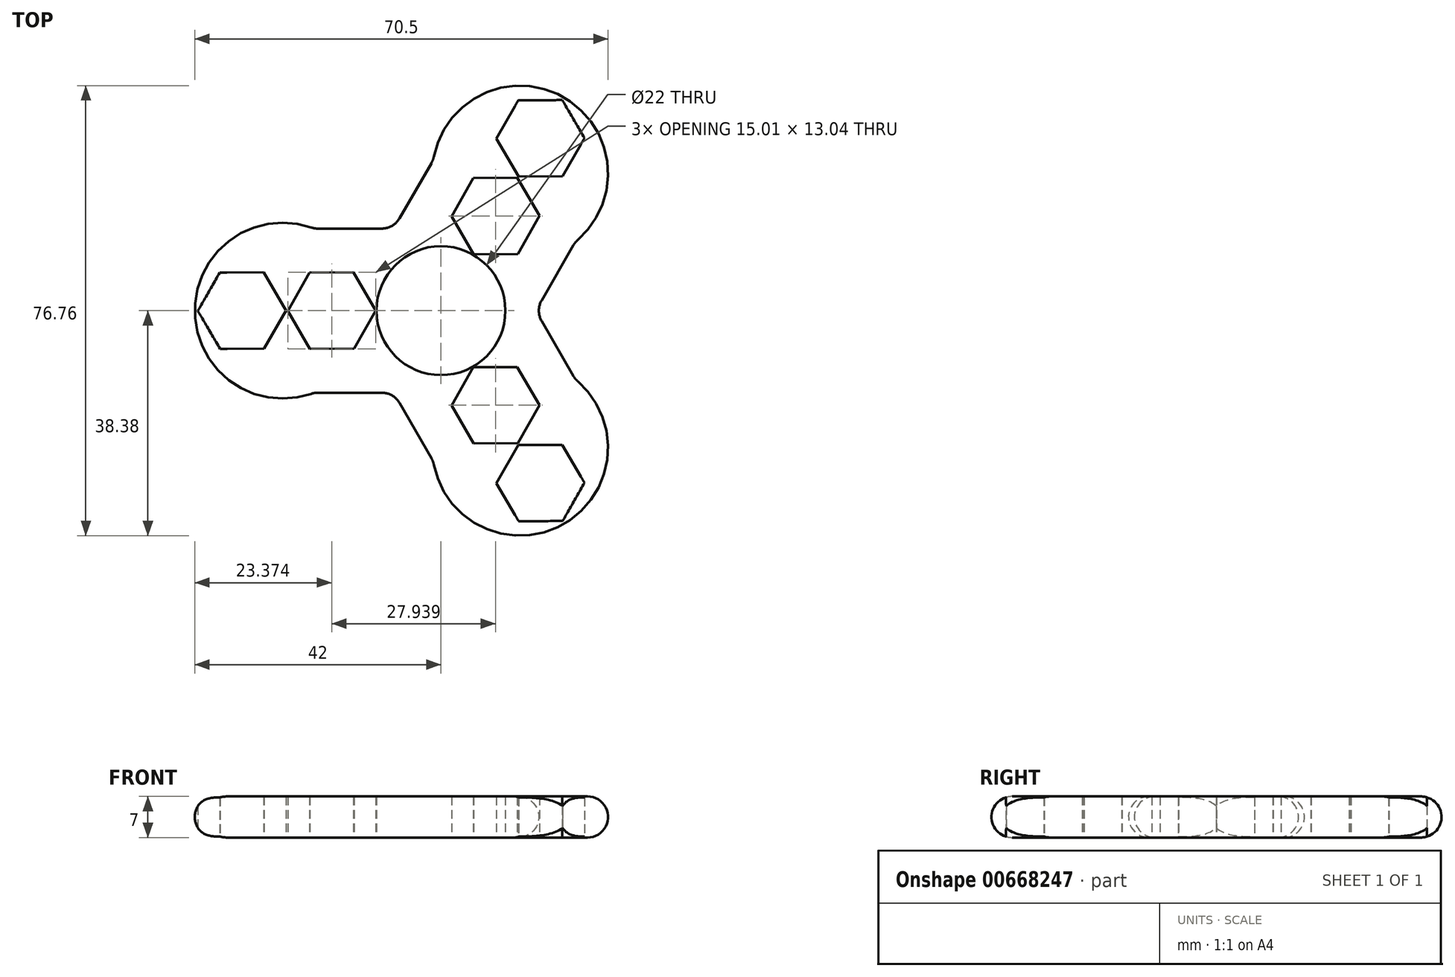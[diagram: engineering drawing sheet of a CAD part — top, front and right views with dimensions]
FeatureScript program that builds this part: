
annotation { "Feature Type Name" : "Feature", "Feature Type Description" : "" }
export const myFeature = defineFeature(function(context is Context, id is Id, definition is map)
    precondition{}
    {
        {
            var Q0;
            Q0=qCreatedBy(makeId("Front.planeOp"),FACE);
            var sketch = newSketch(context, id + "F0", { "sketchPlane" : qUnion([Q0])});
            skLineSegment(sketch, "E0", {"start": v(0, 0) * mm, "end": v(0, 6.18) * mm});
            skSolve(sketch);
        }
        {
            var Q0;
            Q0=qCreatedBy(makeId("Top.planeOp"),FACE);
            var sketch = newSketch(context, id + "F1", { "sketchPlane" : qUnion([Q0])});
            skArc(sketch, "E1", {"start": v(0, 11) * mm, "mid": v(-11, 0) * mm, "end": v(0, -11) * mm});
            skLineSegment(sketch, "E2", {"start": v(0, 56.07) * mm, "end": v(0, 11) * mm, "construction": true});
            skLineSegment(sketch, "E3", {"start": v(-42, 56.32) * mm, "end": v(-42, -55.95) * mm, "construction": true});
            skArc(sketch, "E4", {"start": v(-21.61, 14) * mm, "mid": v(-42, 0) * mm, "end": v(-21.61, -14) * mm});
            skLineSegment(sketch, "E5", {"start": v(0, 14) * mm, "end": v(-21.61, 14) * mm});
            skLineSegment(sketch, "E6", {"start": v(0, -14) * mm, "end": v(-21.61, -14) * mm});
            skLineSegment(sketch, "E7", {"start": v(0, 14) * mm, "end": v(0, 11) * mm});
            skLineSegment(sketch, "E8.trimOffspring", {"start": v(0, -11) * mm, "end": v(0, -55.82) * mm, "construction": true});
            skLineSegment(sketch, "E9.trimOffspring", {"start": v(0, -11) * mm, "end": v(0, -14) * mm});
            skPoint(sketch, "E10.endSnap0", {"position": v(-11, 0) * mm});
            skPoint(sketch, "E11", {"position": v(-33.95, 0) * mm});
            skCircle(sketch, "E12.cCircle", {"center": v(-33.95, 0) * mm, "radius": 6.5 * mm, "construction": true});
            skLineSegment(sketch, "E12.0", {"start": v(-37.67, -6.52) * mm, "end": v(-41.46, -0.04) * mm});
            skLineSegment(sketch, "E12.1", {"start": v(-41.46, -0.04) * mm, "end": v(-37.74, 6.48) * mm});
            skLineSegment(sketch, "E12.2", {"start": v(-37.74, 6.48) * mm, "end": v(-30.24, 6.52) * mm});
            skLineSegment(sketch, "E12.3", {"start": v(-30.24, 6.52) * mm, "end": v(-26.45, 0.04) * mm});
            skLineSegment(sketch, "E12.4", {"start": v(-26.45, 0.04) * mm, "end": v(-30.16, -6.48) * mm});
            skLineSegment(sketch, "E12.5", {"start": v(-30.16, -6.48) * mm, "end": v(-37.67, -6.52) * mm});
            skPoint(sketch, "E12.0.midPoint", {"position": v(-39.57, -3.28) * mm});
            skPoint(sketch, "E13", {"position": v(-18.63, 0) * mm});
            skCircle(sketch, "E14.cCircle", {"center": v(-18.63, 0) * mm, "radius": 6.5 * mm, "construction": true});
            skLineSegment(sketch, "E14.0", {"start": v(-22.34, -6.52) * mm, "end": v(-26.13, -0.04) * mm});
            skLineSegment(sketch, "E14.1", {"start": v(-26.13, -0.04) * mm, "end": v(-22.42, 6.48) * mm});
            skLineSegment(sketch, "E14.2", {"start": v(-22.42, 6.48) * mm, "end": v(-14.91, 6.52) * mm});
            skLineSegment(sketch, "E14.3", {"start": v(-14.91, 6.52) * mm, "end": v(-11.12, 0.04) * mm});
            skLineSegment(sketch, "E14.4", {"start": v(-11.12, 0.04) * mm, "end": v(-14.84, -6.48) * mm});
            skLineSegment(sketch, "E14.5", {"start": v(-14.84, -6.48) * mm, "end": v(-22.34, -6.52) * mm});
            skSolve(sketch);
        }
        {
            var Q0;
            Q0=makeQuery(id+"F1.imprint","IMPRINT",FACE,{"disambiguationData":[TD([[makeQuery(id+"F1.imprint","IMPRINT",EDGE,{"derivedFrom":sQuery(id+"F1.wireOp",EDGE,"E1")}),-1.0]])]});
            extrude(context, id + "F2", {"entities" : qUnion([Q0]), "depth" : 7 * mm, "offsetDistance" : 25 * mm});
        }
        {
            var Q0;
            Q0=makeQuery(id+"F2.opExtrude","SWEPT_BODY",BODY,{"disambiguationData":[OSD([sQuery(id+"F1.wireOp",EDGE,"E1"),sQuery(id+"F1.wireOp",EDGE,"E4"),sQuery(id+"F1.wireOp",EDGE,"E5"),sQuery(id+"F1.wireOp",EDGE,"E6"),sQuery(id+"F1.wireOp",EDGE,"E7"),sQuery(id+"F1.wireOp",EDGE,"E9.trimOffspring"),sQuery(id+"F1.wireOp",EDGE,"E12.0"),sQuery(id+"F1.wireOp",EDGE,"E12.1"),sQuery(id+"F1.wireOp",EDGE,"E12.2"),sQuery(id+"F1.wireOp",EDGE,"E12.3"),sQuery(id+"F1.wireOp",EDGE,"E12.4"),sQuery(id+"F1.wireOp",EDGE,"E12.5"),sQuery(id+"F1.wireOp",EDGE,"E14.0"),sQuery(id+"F1.wireOp",EDGE,"E14.1"),sQuery(id+"F1.wireOp",EDGE,"E14.2"),sQuery(id+"F1.wireOp",EDGE,"E14.3"),sQuery(id+"F1.wireOp",EDGE,"E14.4"),sQuery(id+"F1.wireOp",EDGE,"E14.5")])]});
            var Q1;
            Q1=sQuery(id+"F0.wireOp",EDGE,"E0");
            circularPattern(context, id + "F3", {"operationType" : NewBodyOperationType.ADD, "entities" : qUnion([Q0]), "axis" : qUnion([Q1]), "angle" : 240 * degree, "instanceCount" : 3, "equalSpace" : true});
        }
        {
            var Q0;
            Q0=makeQuery(id+"F2.opExtrude","SWEPT_EDGE",EDGE,{"disambiguationData":[OSD([sQuery(id+"F1.wireOp",EDGE,"E4"),sQuery(id+"F1.wireOp",EDGE,"E6")])]});
            var Q1;
            Q1=makeQuery(id+"F3.boolean.opBoolean","INTERSECT",EDGE,{"derivedFrom":[makeQuery(id+"F2.opExtrude","SWEPT_FACE",FACE,{"disambiguationData":[OSD([sQuery(id+"F1.wireOp",EDGE,"E6")])]}),makeQuery(id+"F3.opPattern","COPY",FACE,{"derivedFrom":makeQuery(id+"F2.opExtrude","SWEPT_FACE",FACE,{"disambiguationData":[OSD([sQuery(id+"F1.wireOp",EDGE,"E5")])]}),"instanceName":"1"})]});
            var Q2;
            Q2=makeQuery(id+"F3.opPattern","COPY",EDGE,{"derivedFrom":makeQuery(id+"F2.opExtrude","SWEPT_EDGE",EDGE,{"disambiguationData":[OSD([sQuery(id+"F1.wireOp",EDGE,"E4"),sQuery(id+"F1.wireOp",EDGE,"E5")])]}),"instanceName":"1"});
            var Q3;
            Q3=makeQuery(id+"F3.opPattern","COPY",EDGE,{"derivedFrom":makeQuery(id+"F2.opExtrude","SWEPT_EDGE",EDGE,{"disambiguationData":[OSD([sQuery(id+"F1.wireOp",EDGE,"E4"),sQuery(id+"F1.wireOp",EDGE,"E6")])]}),"instanceName":"1"});
            var Q4;
            Q4=makeQuery(id+"F3.boolean.opBoolean","INTERSECT",EDGE,{"derivedFrom":[makeQuery(id+"F3.opPattern","COPY",FACE,{"derivedFrom":makeQuery(id+"F2.opExtrude","SWEPT_FACE",FACE,{"disambiguationData":[OSD([sQuery(id+"F1.wireOp",EDGE,"E6")])]}),"instanceName":"1"}),makeQuery(id+"F3.opPattern","COPY",FACE,{"derivedFrom":makeQuery(id+"F2.opExtrude","SWEPT_FACE",FACE,{"disambiguationData":[OSD([sQuery(id+"F1.wireOp",EDGE,"E5")])]}),"instanceName":"2"})]});
            var Q5;
            Q5=makeQuery(id+"F3.opPattern","COPY",EDGE,{"derivedFrom":makeQuery(id+"F2.opExtrude","SWEPT_EDGE",EDGE,{"disambiguationData":[OSD([sQuery(id+"F1.wireOp",EDGE,"E4"),sQuery(id+"F1.wireOp",EDGE,"E5")])]}),"instanceName":"2"});
            var Q6;
            Q6=makeQuery(id+"F3.opPattern","COPY",EDGE,{"derivedFrom":makeQuery(id+"F2.opExtrude","SWEPT_EDGE",EDGE,{"disambiguationData":[OSD([sQuery(id+"F1.wireOp",EDGE,"E4"),sQuery(id+"F1.wireOp",EDGE,"E6")])]}),"instanceName":"2"});
            var Q7;
            Q7=makeQuery(id+"F3.boolean.opBoolean","INTERSECT",EDGE,{"derivedFrom":[makeQuery(id+"F2.opExtrude","SWEPT_FACE",FACE,{"disambiguationData":[OSD([sQuery(id+"F1.wireOp",EDGE,"E5")])]}),makeQuery(id+"F3.opPattern","COPY",FACE,{"derivedFrom":makeQuery(id+"F2.opExtrude","SWEPT_FACE",FACE,{"disambiguationData":[OSD([sQuery(id+"F1.wireOp",EDGE,"E6")])]}),"instanceName":"2"})]});
            var Q8;
            Q8=makeQuery(id+"F2.opExtrude","SWEPT_EDGE",EDGE,{"disambiguationData":[OSD([sQuery(id+"F1.wireOp",EDGE,"E4"),sQuery(id+"F1.wireOp",EDGE,"E5")])]});
            var Q9;
            Q9=makeQuery(id+"F3.opPattern","COPY",EDGE,{"derivedFrom":makeQuery(id+"F2.opExtrude","CAP_EDGE",EDGE,{"disambiguationData":[OSD([sQuery(id+"F1.wireOp",EDGE,"E4")])],"isStart":false}),"instanceName":"2"});
            var Q10;
            Q10=makeQuery(id+"F3.opPattern","COPY",EDGE,{"derivedFrom":makeQuery(id+"F2.opExtrude","CAP_EDGE",EDGE,{"disambiguationData":[OSD([sQuery(id+"F1.wireOp",EDGE,"E4")])],"isStart":true}),"instanceName":"2"});
            var Q11;
            Q11=makeQuery(id+"F3.opPattern","COPY",EDGE,{"derivedFrom":makeQuery(id+"F2.opExtrude","CAP_EDGE",EDGE,{"disambiguationData":[OSD([sQuery(id+"F1.wireOp",EDGE,"E6")])],"isStart":true}),"instanceName":"2"});
            var Q12;
            Q12=makeQuery(id+"F3.opPattern","COPY",EDGE,{"derivedFrom":makeQuery(id+"F2.opExtrude","CAP_EDGE",EDGE,{"disambiguationData":[OSD([sQuery(id+"F1.wireOp",EDGE,"E6")])],"isStart":false}),"instanceName":"2"});
            var Q13;
            Q13=makeQuery(id+"F2.opExtrude","CAP_EDGE",EDGE,{"disambiguationData":[OSD([sQuery(id+"F1.wireOp",EDGE,"E5")])],"isStart":false});
            var Q14;
            Q14=makeQuery(id+"F2.opExtrude","CAP_EDGE",EDGE,{"disambiguationData":[OSD([sQuery(id+"F1.wireOp",EDGE,"E5")])],"isStart":true});
            var Q15;
            Q15=makeQuery(id+"F2.opExtrude","CAP_EDGE",EDGE,{"disambiguationData":[OSD([sQuery(id+"F1.wireOp",EDGE,"E4")])],"isStart":true});
            var Q16;
            Q16=makeQuery(id+"F2.opExtrude","CAP_EDGE",EDGE,{"disambiguationData":[OSD([sQuery(id+"F1.wireOp",EDGE,"E4")])],"isStart":false});
            var Q17;
            Q17=makeQuery(id+"F2.opExtrude","CAP_EDGE",EDGE,{"disambiguationData":[OSD([sQuery(id+"F1.wireOp",EDGE,"E6")])],"isStart":false});
            var Q18;
            Q18=makeQuery(id+"F2.opExtrude","CAP_EDGE",EDGE,{"disambiguationData":[OSD([sQuery(id+"F1.wireOp",EDGE,"E6")])],"isStart":true});
            var Q19;
            Q19=makeQuery(id+"F3.opPattern","COPY",EDGE,{"derivedFrom":makeQuery(id+"F2.opExtrude","CAP_EDGE",EDGE,{"disambiguationData":[OSD([sQuery(id+"F1.wireOp",EDGE,"E5")])],"isStart":true}),"instanceName":"1"});
            var Q20;
            Q20=makeQuery(id+"F3.opPattern","COPY",EDGE,{"derivedFrom":makeQuery(id+"F2.opExtrude","CAP_EDGE",EDGE,{"disambiguationData":[OSD([sQuery(id+"F1.wireOp",EDGE,"E5")])],"isStart":false}),"instanceName":"1"});
            var Q21;
            Q21=makeQuery(id+"F3.opPattern","COPY",EDGE,{"derivedFrom":makeQuery(id+"F2.opExtrude","CAP_EDGE",EDGE,{"disambiguationData":[OSD([sQuery(id+"F1.wireOp",EDGE,"E4")])],"isStart":false}),"instanceName":"1"});
            var Q22;
            Q22=makeQuery(id+"F3.opPattern","COPY",EDGE,{"derivedFrom":makeQuery(id+"F2.opExtrude","CAP_EDGE",EDGE,{"disambiguationData":[OSD([sQuery(id+"F1.wireOp",EDGE,"E4")])],"isStart":true}),"instanceName":"1"});
            var Q23;
            Q23=makeQuery(id+"F3.opPattern","COPY",EDGE,{"derivedFrom":makeQuery(id+"F2.opExtrude","CAP_EDGE",EDGE,{"disambiguationData":[OSD([sQuery(id+"F1.wireOp",EDGE,"E5")])],"isStart":true}),"instanceName":"2"});
            var Q24;
            Q24=makeQuery(id+"F3.opPattern","COPY",EDGE,{"derivedFrom":makeQuery(id+"F2.opExtrude","CAP_EDGE",EDGE,{"disambiguationData":[OSD([sQuery(id+"F1.wireOp",EDGE,"E5")])],"isStart":false}),"instanceName":"2"});
            var Q25;
            Q25=makeQuery(id+"F3.opPattern","COPY",EDGE,{"derivedFrom":makeQuery(id+"F2.opExtrude","CAP_EDGE",EDGE,{"disambiguationData":[OSD([sQuery(id+"F1.wireOp",EDGE,"E6")])],"isStart":true}),"instanceName":"1"});
            var Q26;
            Q26=makeQuery(id+"F3.opPattern","COPY",EDGE,{"derivedFrom":makeQuery(id+"F2.opExtrude","CAP_EDGE",EDGE,{"disambiguationData":[OSD([sQuery(id+"F1.wireOp",EDGE,"E6")])],"isStart":false}),"instanceName":"1"});
            fillet(context, id + "F4", {"entities" : qUnion([Q0, Q1, Q2, Q3, Q4, Q5, Q6, Q7, Q8, Q9, Q10, Q11, Q12, Q13, Q14, Q15, Q16, Q17, Q18, Q19, Q20, Q21, Q22, Q23, Q24, Q25, Q26]), "radius" : 3.5 * mm, "tangentPropagation" : true, "allowEdgeOverflow" : false});
        }
    });
